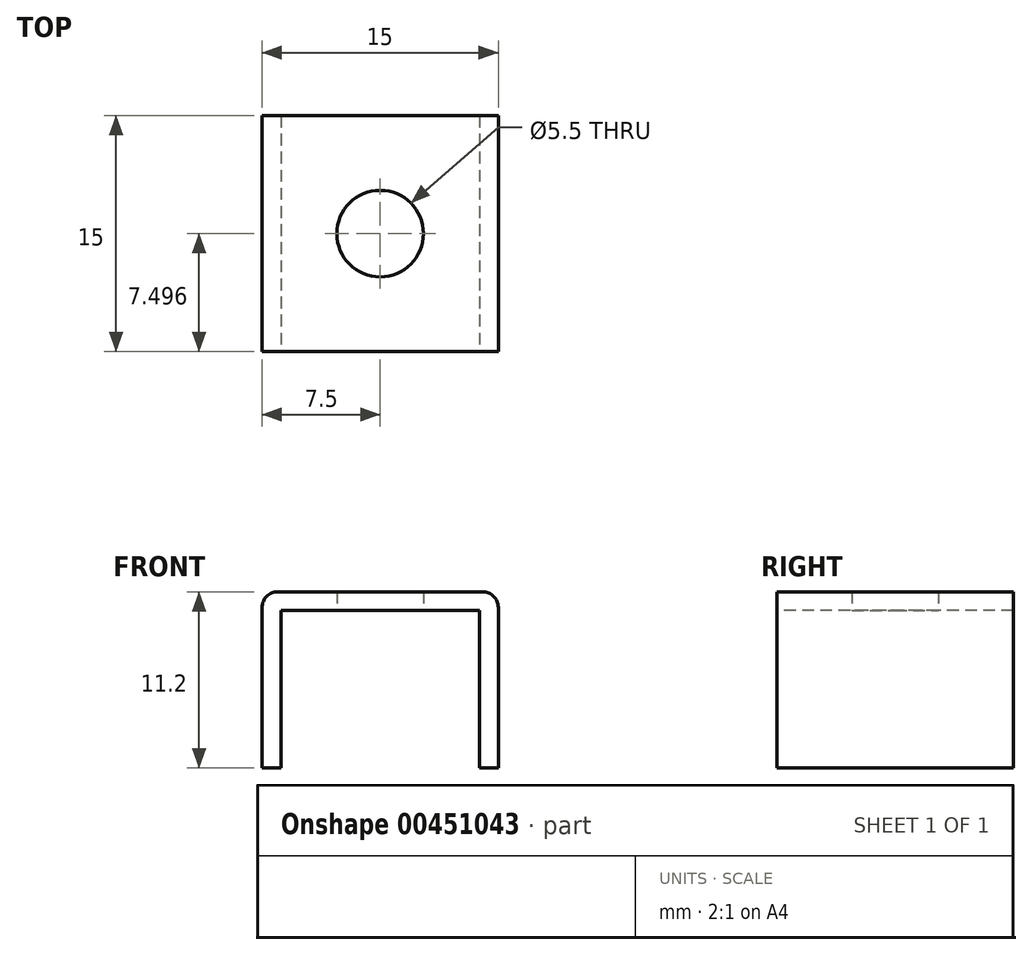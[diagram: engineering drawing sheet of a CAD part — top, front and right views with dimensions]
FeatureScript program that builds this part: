
annotation { "Feature Type Name" : "Feature", "Feature Type Description" : "" }
export const myFeature = defineFeature(function(context is Context, id is Id, definition is map)
    precondition{}
    {
        {
            var Q0;
            Q0=qCreatedBy(makeId("Top.planeOp"),FACE);
            var sketch = newSketch(context, id + "F0", { "sketchPlane" : qUnion([Q0])});
            skLineSegment(sketch, "E0.bottom", {"start": v(-15, -19.44) * mm, "end": v(0, -19.44) * mm});
            skLineSegment(sketch, "E0.top", {"start": v(-15, -34.44) * mm, "end": v(0, -34.44) * mm});
            skLineSegment(sketch, "E0.left", {"start": v(-15, -19.44) * mm, "end": v(-15, -34.44) * mm});
            skLineSegment(sketch, "E0.right", {"start": v(0, -19.44) * mm, "end": v(0, -34.44) * mm});
            skPoint(sketch, "E1.endSnap0", {"position": v(-7.5, -26.94) * mm});
            skSolve(sketch);
        }
        {
            var Q0;
            Q0=makeQuery(id+"F0.imprint","IMPRINT",FACE,{"disambiguationData":[TD([[makeQuery(id+"F0.imprint","IMPRINT",EDGE,{"derivedFrom":sQuery(id+"F0.wireOp",EDGE,"E0.bottom")}),-1.0]])]});
            var sketch = newSketch(context, id + "F1", { "sketchPlane" : qUnion([Q0])});
            skSolve(sketch);
        }
        {
            var Q0;
            Q0=makeQuery(id+"F0.imprint","IMPRINT",FACE,{"disambiguationData":[TD([[makeQuery(id+"F0.imprint","IMPRINT",EDGE,{"derivedFrom":sQuery(id+"F0.wireOp",EDGE,"E0.bottom")}),-1.0]])]});
            extrude(context, id + "F2", {"entities" : qUnion([Q0]), "depth" : 1.2 * mm});
        }
        {
            var Q0;
            Q0=makeQuery(id+"F1.imprint","IMPRINT",FACE,{"disambiguationData":[TD([[makeQuery(id+"F1.imprint","IMPRINT",EDGE,{"derivedFrom":makeQuery(id+"F0.imprint","IMPRINT",EDGE,{"derivedFrom":sQuery(id+"F0.wireOp",EDGE,"E0.bottom")})}),-1.0]])]});
            var sketch = newSketch(context, id + "F3", { "sketchPlane" : qUnion([Q0])});
            skLineSegment(sketch, "E2.0", {"start": v(-1.2, -19.44) * mm, "end": v(-1.2, -34.44) * mm});
            skLineSegment(sketch, "E3.0", {"start": v(-13.8, -19.44) * mm, "end": v(-13.8, -34.44) * mm});
            skLineSegment(sketch, "E4.0", {"start": v(-15, -19.44) * mm, "end": v(-15, -34.44) * mm});
            skLineSegment(sketch, "E5.0", {"start": v(0, -19.44) * mm, "end": v(0, -34.44) * mm});
            skLineSegment(sketch, "E6", {"start": v(-15, -34.44) * mm, "end": v(-13.8, -34.44) * mm});
            skLineSegment(sketch, "E7", {"start": v(-15, -19.44) * mm, "end": v(-13.8, -19.44) * mm});
            skLineSegment(sketch, "E8", {"start": v(-1.2, -19.44) * mm, "end": v(0, -19.44) * mm});
            skLineSegment(sketch, "E9", {"start": v(-1.2, -34.44) * mm, "end": v(0, -34.44) * mm});
            skSolve(sketch);
        }
        {
            var Q0;
            Q0=makeQuery(id+"F3.imprint","IMPRINT",FACE,{"disambiguationData":[TD([[makeQuery(id+"F3.imprint","IMPRINT",EDGE,{"derivedFrom":sQuery(id+"F3.wireOp",EDGE,"E2.0")}),1.0]])]});
            var Q1;
            Q1=makeQuery(id+"F3.imprint","IMPRINT",FACE,{"disambiguationData":[TD([[makeQuery(id+"F3.imprint","IMPRINT",EDGE,{"derivedFrom":sQuery(id+"F3.wireOp",EDGE,"E3.0")}),-1.0]])]});
            extrude(context, id + "F4", {"entities" : qUnion([Q0, Q1]), "operationType" : NewBodyOperationType.ADD, "oppositeDirection" : true, "depth" : 10 * mm});
        }
        {
            var Q0;
            Q0=makeQuery(id+"F2.opExtrude","CAP_EDGE",EDGE,{"disambiguationData":[OSD([sQuery(id+"F0.wireOp",EDGE,"E0.left")])],"isStart":false});
            var Q1;
            Q1=makeQuery(id+"F2.opExtrude","CAP_EDGE",EDGE,{"disambiguationData":[OSD([sQuery(id+"F0.wireOp",EDGE,"E0.right")])],"isStart":false});
            var Q2;
            Q2=makeQuery(id+"F4.opExtrude","CAP_EDGE",EDGE,{"disambiguationData":[OSD([sQuery(id+"F3.wireOp",EDGE,"E2.0")])],"isStart":true});
            var Q3;
            Q3=makeQuery(id+"F4.opExtrude","CAP_EDGE",EDGE,{"disambiguationData":[OSD([sQuery(id+"F3.wireOp",EDGE,"E3.0")])],"isStart":true});
            fillet(context, id + "F5", {"entities" : qUnion([Q0, Q1, Q2, Q3]), "radius" : 1 * mm, "tangentPropagation" : true, "allowEdgeOverflow" : false});
        }
        {
            var Q0;
            Q0=sQuery(id+"F0.wireOp",VERTEX,"E1.endSnap0");
            var Q1;
            Q1=makeQuery(id+"F2.opExtrude","SWEPT_BODY",BODY,{"disambiguationData":[OSD([sQuery(id+"F0.wireOp",EDGE,"E0.bottom"),sQuery(id+"F0.wireOp",EDGE,"E0.top"),sQuery(id+"F0.wireOp",EDGE,"E0.left"),sQuery(id+"F0.wireOp",EDGE,"E0.right")])]});
            hole(context, id + "F6", {"style" : HoleStyle.SIMPLE, "endStyle" : HoleEndStyle.THROUGH, "oppositeDirection" : true, "standardTappedOrClearance" : lookupTablePath({ "standard" : "ISO", "fit" : "Normal", "size" : "M5", "type" : "Clearance" }), "standardBlindInLast" : lookupTablePath({ "fit" : "Standard", "standard" : "ISO", "size" : "M5", "type" : "Clearance" }), "holeDiameter" : 5.5 * mm, "isTappedThrough" : true, "tappedDepth" : 12 * mm, "tapClearance" : 3, "locations" : qUnion([Q0]), "scope" : qUnion([Q1])});
        }
    });
